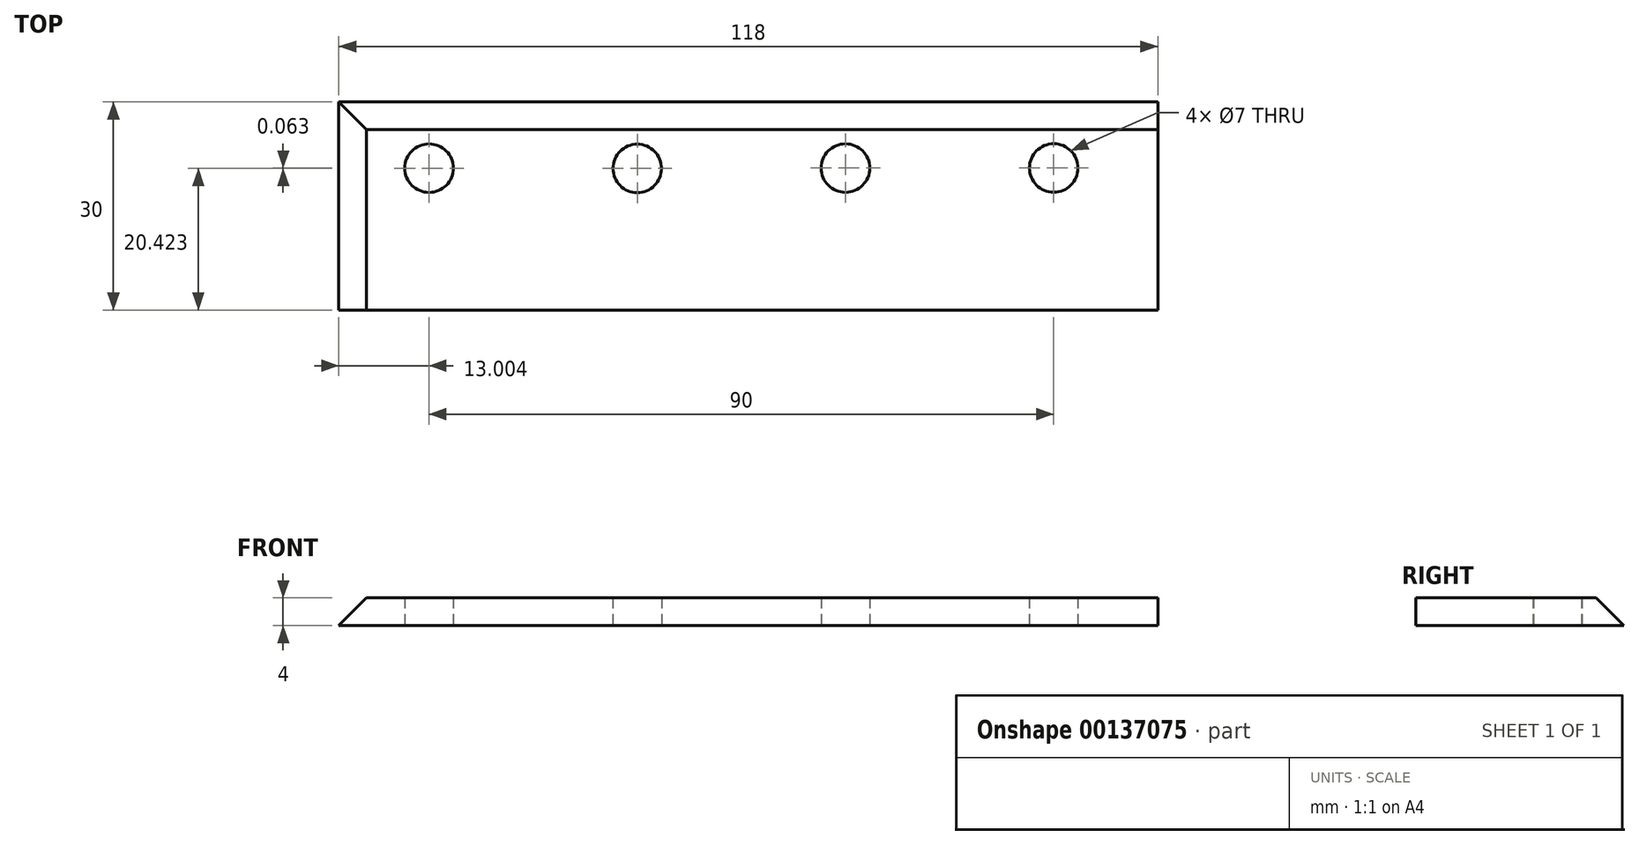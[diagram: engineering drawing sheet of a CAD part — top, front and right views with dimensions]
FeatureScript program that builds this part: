
annotation { "Feature Type Name" : "Feature", "Feature Type Description" : "" }
export const myFeature = defineFeature(function(context is Context, id is Id, definition is map)
    precondition{}
    {
        {
            var Q0;
            Q0=qCreatedBy(makeId("Top.planeOp"),FACE);
            var sketch = newSketch(context, id + "F0", { "sketchPlane" : qUnion([Q0])});
            skLineSegment(sketch, "E0", {"start": v(-73.54, 0) * mm, "end": v(-73.54, -30) * mm});
            skLineSegment(sketch, "E1", {"start": v(-73.54, -30) * mm, "end": v(44.46, -30) * mm});
            skLineSegment(sketch, "E2", {"start": v(44.46, -30) * mm, "end": v(44.46, 0) * mm});
            skCircle(sketch, "E3", {"center": v(-60.54, -9.53) * mm, "radius": 3.5 * mm});
            skCircle(sketch, "E4", {"center": v(-30.54, -9.58) * mm, "radius": 3.5 * mm});
            skCircle(sketch, "E5", {"center": v(-0.54, -9.53) * mm, "radius": 3.5 * mm});
            skCircle(sketch, "E6", {"center": v(29.46, -9.51) * mm, "radius": 3.5 * mm});
            skLineSegment(sketch, "E7", {"start": v(-73.54, 0) * mm, "end": v(-73.54, -4) * mm});
            skLineSegment(sketch, "E8", {"start": v(-60.54, 0) * mm, "end": v(-60.54, -30) * mm});
            skLineSegment(sketch, "E9", {"start": v(-60.54, 0) * mm, "end": v(-73.54, 0) * mm});
            skLineSegment(sketch, "E10", {"start": v(-60.54, 0) * mm, "end": v(44.46, 0) * mm});
            skLineSegment(sketch, "E11", {"start": v(-0.54, -6.03) * mm, "end": v(-0.54, -13.03) * mm, "construction": true});
            skLineSegment(sketch, "E12", {"start": v(-52.7, -30) * mm, "end": v(-52.7, -4) * mm});
            skSolve(sketch);
        }
        {
            var Q0;
            Q0=qSketchRegion(id+"F0",true);
            extrude(context, id + "F1", {"entities" : qUnion([Q0]), "depth" : 4 * mm});
        }
        {
            var Q0;
            Q0=makeQuery(id+"F1.opExtrude","CAP_EDGE",EDGE,{"disambiguationData":[OSD([sQuery(id+"F0.wireOp",EDGE,"E0"),sQuery(id+"F0.wireOp",EDGE,"E7")])],"isStart":false});
            var Q1;
            Q1=makeQuery(id+"F1.opExtrude","CAP_EDGE",EDGE,{"disambiguationData":[OSD([sQuery(id+"F0.wireOp",EDGE,"E9"),sQuery(id+"F0.wireOp",EDGE,"E10")])],"isStart":false});
            chamfer(context, id + "F2", {"entities" : qUnion([Q0, Q1]), "width" : 4 * mm, "tangentPropagation" : true});
        }
    });
